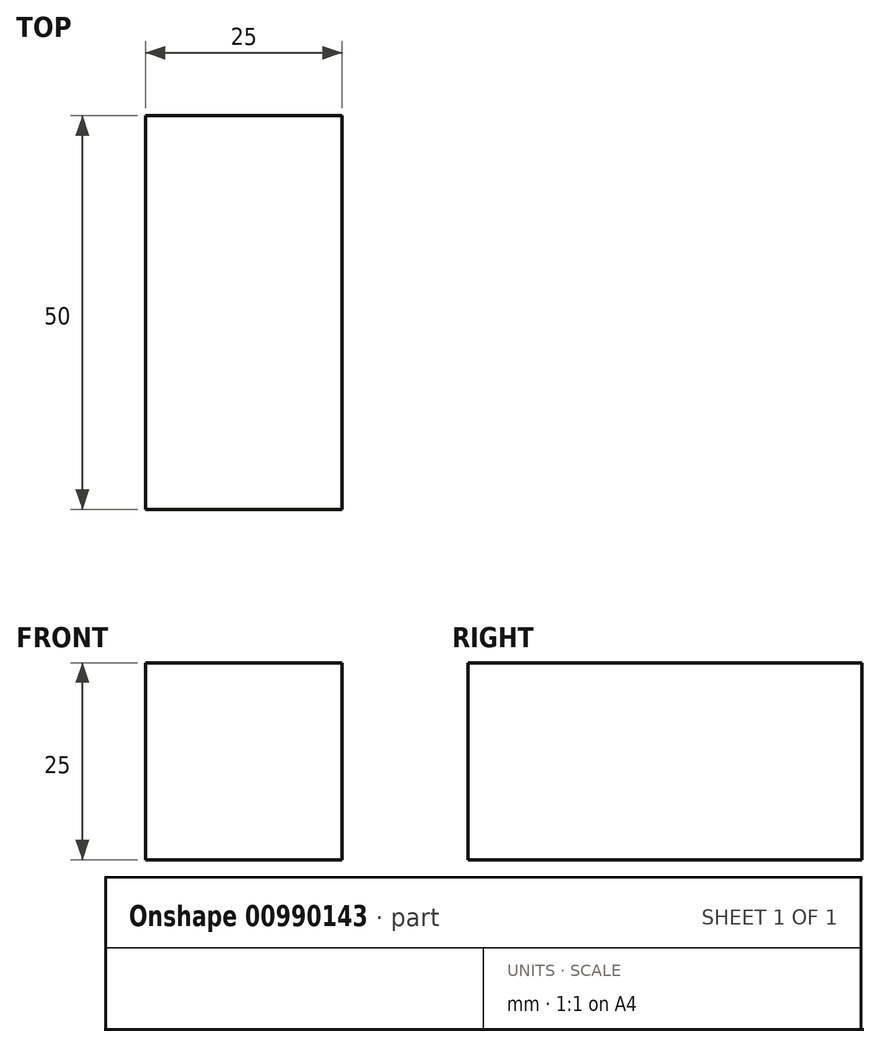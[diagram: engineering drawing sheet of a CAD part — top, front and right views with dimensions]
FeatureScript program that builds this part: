
annotation { "Feature Type Name" : "Feature", "Feature Type Description" : "" }
export const myFeature = defineFeature(function(context is Context, id is Id, definition is map)
    precondition{}
    {
        {
            var Q0;
            Q0=qCreatedBy(makeId("Top.planeOp"),FACE);
            var sketch = newSketch(context, id + "F0", { "sketchPlane" : qUnion([Q0])});
            skLineSegment(sketch, "E0.bottom", {"start": v(-12.5, -12.5) * mm, "end": v(12.5, -12.5) * mm});
            skLineSegment(sketch, "E0.top", {"start": v(-12.5, 12.5) * mm, "end": v(12.5, 12.5) * mm});
            skLineSegment(sketch, "E0.left", {"start": v(-12.5, -12.5) * mm, "end": v(-12.5, 12.5) * mm});
            skLineSegment(sketch, "E0.right", {"start": v(12.5, -12.5) * mm, "end": v(12.5, 12.5) * mm});
            skSolve(sketch);
        }
        {
            var Q0;
            Q0=makeQuery(id+"F0.imprint","IMPRINT",FACE,{"disambiguationData":[TD([[makeQuery(id+"F0.imprint","IMPRINT",EDGE,{"derivedFrom":sQuery(id+"F0.wireOp",EDGE,"E0.bottom")}),1.0]])]});
            extrude(context, id + "F1", {"entities" : qUnion([Q0]), "endBound" : BoundingType.SYMMETRIC, "depth" : 25 * mm, "offsetDistance" : 25 * mm});
        }
        {
            var Q0;
            Q0=makeQuery(id+"F1.opExtrude","SWEPT_FACE",FACE,{"disambiguationData":[OSD([sQuery(id+"F0.wireOp",EDGE,"E0.bottom")])]});
            extrude(context, id + "F2", {"entities" : qUnion([Q0]), "operationType" : NewBodyOperationType.ADD, "depth" : 25 * mm, "offsetDistance" : 25 * mm});
        }
    });
